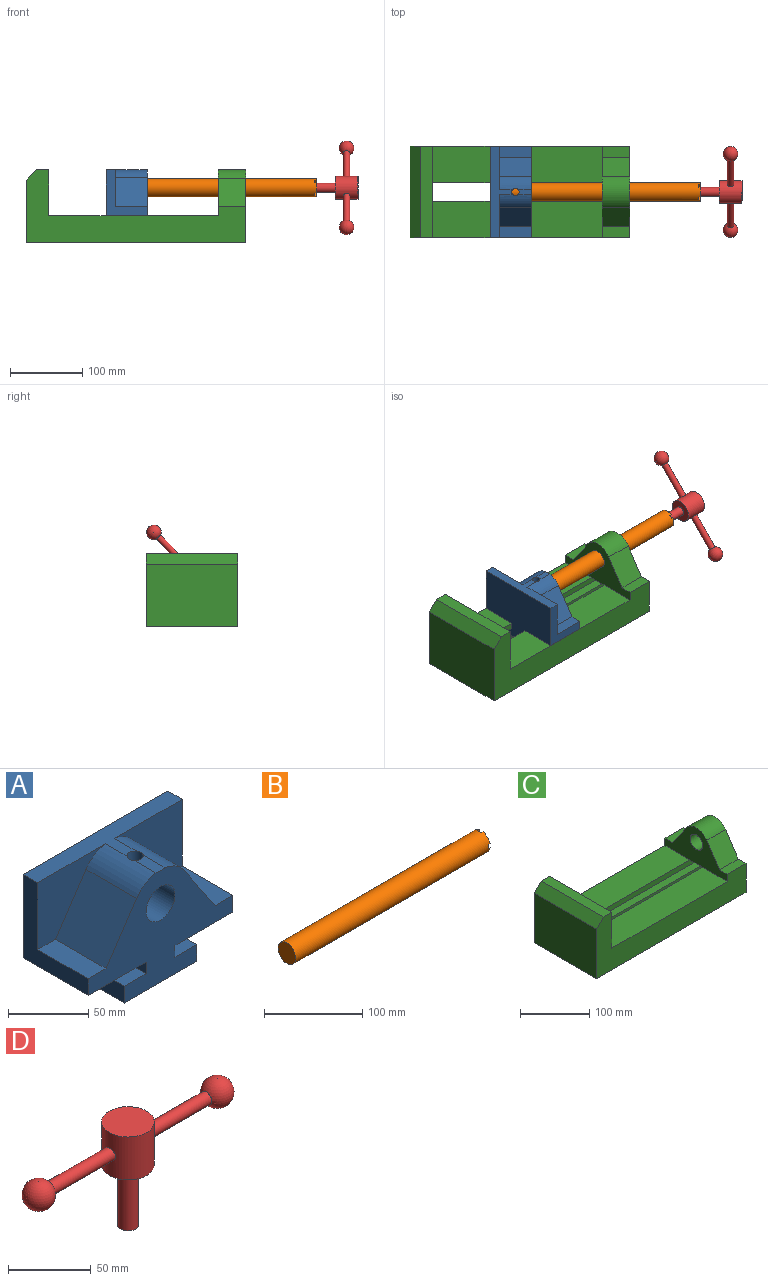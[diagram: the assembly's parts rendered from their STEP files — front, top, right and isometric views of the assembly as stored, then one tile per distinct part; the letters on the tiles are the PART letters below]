
ASSEMBLY  parts=4 mates=3
PART A: 26 faces, bbox 127x57.2x85.1 mm
  f0: plane 127x31.76mm, normal (0,0,1), area 1753.7mm2, adj f2,f3,f14,f15,f18,f20,f22,f25
  f1: plane 19.06x7.94mm, normal (0,0,1), area 140.8mm2, adj f13,f15,f20,f25
  f2: plane 63.5x57.15mm, normal (-1,0,0), area 1371mm2, adj f0,f4,f13,f14,f21,f22
  f3: plane 63.5x57.15mm, normal (1,0,0), area 1371mm2, adj f0,f12,f13,f14,f17,f18
  f4: plane 57.15x50.8mm, normal (0,0,-1), area 2903.2mm2, adj f2,f5,f13,f14
  f5: plane 57.15x8.89mm, normal (-1,0,0), area 508.1mm2, adj f4,f6,f13,f14
  f6: plane 57.15x19.05mm, normal (0,0,1), area 1088.7mm2, adj f5,f7,f13,f14
  f7: plane 57.15x12.7mm, normal (-1,0,0), area 725.8mm2, adj f6,f8,f13,f14
  f8: plane 63.5x57.15mm, normal (0,0,-1), area 3629mm2, adj f7,f9,f13,f14
  f9: plane 57.15x12.7mm, normal (1,0,0), area 725.8mm2, adj f8,f10,f13,f14
  f10: plane 57.15x19.05mm, normal (0,0,1), area 1088.7mm2, adj f9,f11,f13,f14
  f11: plane 57.15x8.89mm, normal (1,0,0), area 508.1mm2, adj f10,f12,f13,f14
  f12: plane 57.15x50.8mm, normal (0,0,-1), area 2903.2mm2, adj f3,f11,f13,f14
  f13: plane 127x85.09mm, normal (0,-1,0), area 5219.4mm2, adj f1,f2,f3,f4,f5,f6,f7,f8
  f14: plane 127x85.09mm, normal (0,1,0), area 9096.8mm2, adj f0,f2,f3,f4,f5,f6,f7,f8
  f15: cylinder r=25.4mm len=44.45mm, axis (0,-1,0), area 923.6mm2, adj f0,f1,f13,f16,f18,f25
  f16: plane 44.45x39.87mm, normal (0.83,0,0.56), area 2135mm2, adj f13,f15,f17,f18
  f17: plane 44.45x15.63mm, normal (0,0,1), area 694.9mm2, adj f3,f13,f16,f18
  f18: plane 59.53x50.8mm, normal (0,-1,0), area 1685.3mm2, adj f0,f3,f15,f16,f17
  f19: plane 44.45x39.87mm, normal (-0.83,0,0.56), area 2135mm2, adj f13,f20,f21,f22
  f20: cylinder r=25.4mm len=44.45mm, axis (0,-1,0), area 923.6mm2, adj f0,f1,f13,f19,f22,f25
  f21: plane 44.45x15.63mm, normal (0,0,1), area 694.9mm2, adj f2,f13,f19,f22
  f22: plane 59.53x50.8mm, normal (0,-1,0), area 1685.3mm2, adj f0,f2,f19,f20,f21
  f23: cylinder r=12.7mm len=44.45mm, axis (0,-1,0), area 3464.1mm2, adj f13,f24,f25
  f24: plane 25.4x25.4mm, normal (0,-1,0), area 506.7mm2, adj f23
  f25: cylinder r=5.08mm len=13.45mm, axis (0,0,1), area 410.4mm2, adj f0,f1,f15,f20,f23
PART B: 20 faces, bbox 279.4x25.4x25.4 mm
  f0: plane 9.9x9.9mm, normal (1,0,0), area 62.3mm2, adj f3,f6,f12,f17
  f1: plane 9.9x9.9mm, normal (1,0,0), area 62.3mm2, adj f3,f6,f14,f18
  f2: plane 9.9x9.9mm, normal (1,0,0), area 62.3mm2, adj f3,f6,f8,f11
  f3: cylinder r=12.7mm len=279.4mm, axis (-1,0,0), area 22243.2mm2, adj f0,f1,f2,f4,f5,f8,f9,f10
  f4: plane 9.9x9.9mm, normal (1,0,0), area 62.3mm2, adj f3,f6,f9,f15
  f5: plane 25.4x25.4mm, normal (-1,0,0), area 506.7mm2, adj f3
  f6: cylinder r=6.35mm len=19.05mm, axis (1,0,0), area 707mm2, adj f0,f1,f2,f4,f7,f8,f9,f10
  f7: plane 12.7x12.7mm, normal (1,0,0), area 126.7mm2, adj f6
  f8: plane 6.62x2.54mm, normal (0,-1,0), area 16.8mm2, adj f2,f3,f6,f10
  f9: plane 6.62x2.54mm, normal (0,1,0), area 16.8mm2, adj f3,f4,f6,f10
  f10: plane 6.88x5.08mm, normal (1,0,0), area 32.7mm2, adj f3,f6,f8,f9
  f11: plane 6.62x2.54mm, normal (0,0,1), area 16.8mm2, adj f2,f3,f6,f13
  f12: plane 6.62x2.54mm, normal (0,0,-1), area 16.8mm2, adj f0,f3,f6,f13
  f13: plane 6.88x5.08mm, normal (1,0,0), area 32.7mm2, adj f3,f6,f11,f12
  f14: plane 6.62x2.54mm, normal (0,0,-1), area 16.8mm2, adj f1,f3,f6,f16
  f15: plane 6.62x2.54mm, normal (0,0,1), area 16.8mm2, adj f3,f4,f6,f16
  f16: plane 6.88x5.08mm, normal (1,0,0), area 32.7mm2, adj f3,f6,f14,f15
  f17: plane 6.62x2.54mm, normal (0,-1,0), area 16.8mm2, adj f0,f3,f6,f19
  f18: plane 6.62x2.54mm, normal (0,1,0), area 16.8mm2, adj f1,f3,f6,f19
  f19: plane 6.88x5.08mm, normal (1,0,0), area 32.7mm2, adj f3,f6,f17,f18
PART C: 28 faces, bbox 304.8x127x101.6 mm
  f0: plane 127x101.6mm, normal (1,0,0), area 7544.1mm2, adj f4,f8,f9,f11,f12,f13,f14,f15
  f1: plane 234.95x50.8mm, normal (0,0,1), area 11935.5mm2, adj f2,f6,f9,f19
  f2: plane 127x63.5mm, normal (-1,0,0), area 4157.1mm2, adj f1,f5,f8,f9,f11,f12,f13,f14
  f3: plane 127x87.31mm, normal (-1,0,0), area 11088.7mm2, adj f4,f8,f9,f10
  f4: plane 304.8x127mm, normal (0,0,-1), area 31774.1mm2, adj f0,f3,f6,f8,f9,f15,f24
  f5: plane 234.95x50.8mm, normal (0,0,1), area 11935.5mm2, adj f2,f6,f8,f20
  f6: plane 127x101.6mm, normal (1,0,0), area 9516.1mm2, adj f1,f4,f5,f7,f8,f9,f15,f16
  f7: plane 127x17.46mm, normal (0,0,1), area 2217.7mm2, adj f6,f8,f9,f10
  f8: plane 304.8x101.6mm, normal (0,-1,0), area 14010.8mm2, adj f0,f2,f3,f4,f5,f6,f7,f10
  f9: plane 304.8x101.6mm, normal (0,1,0), area 14010.8mm2, adj f0,f1,f2,f3,f4,f6,f7,f10
  f10: plane 127x14.29mm, normal (-0.71,0,0.71), area 2566.1mm2, adj f3,f7,f8,f9
  f11: plane 38.1x15.88mm, normal (0,0,1), area 604.8mm2, adj f0,f2,f8,f12
  f12: plane 39.31x38.1mm, normal (0,-0.84,0.55), area 1790.2mm2, adj f0,f2,f11,f13
  f13: cylinder r=25.4mm len=42.88mm, axis (1,0,0), area 1945.5mm2, adj f0,f2,f12,f25
  f14: plane 38.1x25.4mm, normal (0,0,-1), area 967.7mm2, adj f0,f2,f19,f20
  f15: plane 273.05x16.51mm, normal (0,-1,0), area 4508.1mm2, adj f0,f4,f6,f16
  f16: plane 273.05x19.05mm, normal (0,0,1), area 5201.6mm2, adj f0,f6,f15,f17
  f17: plane 273.05x12.7mm, normal (0,-1,0), area 3467.7mm2, adj f0,f6,f16,f18
  f18: plane 273.05x19.05mm, normal (0,0,-1), area 5201.6mm2, adj f0,f6,f17,f19
  f19: plane 273.05x8.89mm, normal (0,-1,0), area 2427.4mm2, adj f0,f1,f6,f14,f18
  f20: plane 273.05x8.89mm, normal (0,1,0), area 2427.4mm2, adj f0,f5,f6,f14,f21
  f21: plane 273.05x19.05mm, normal (0,0,-1), area 5201.6mm2, adj f0,f6,f20,f22
  f22: plane 273.05x12.7mm, normal (0,1,0), area 3467.7mm2, adj f0,f6,f21,f23
  f23: plane 273.05x19.05mm, normal (0,0,1), area 5201.6mm2, adj f0,f6,f22,f24
  f24: plane 273.05x16.51mm, normal (0,1,0), area 4508.1mm2, adj f0,f4,f6,f23
  f25: plane 38.71x38.1mm, normal (0,0.82,0.57), area 1790.2mm2, adj f0,f2,f13,f26
  f26: plane 38.1x15.88mm, normal (0,0,1), area 604.8mm2, adj f0,f2,f9,f25
  f27: cylinder r=12.7mm len=38.1mm, axis (1,0,0), area 3040.2mm2, adj f0,f2
PART D: 9 faces, bbox 172.7x31.8x76.2 mm
  f0: cylinder r=4.45mm len=51.82mm, axis (-1,0,0), area 1438.5mm2, adj f2,f8
  f1: cylinder r=4.45mm len=51.82mm, axis (-1,0,0), area 1438.5mm2, adj f2,f7
  f2: cylinder r=15.88mm len=31.75mm, axis (0,0,-1), area 3041.4mm2, adj f0,f1,f5,f6
  f3: cylinder r=6.35mm len=44.45mm, axis (0,0,-1), area 1773.5mm2, adj f4,f6
  f4: plane 12.7x12.7mm, normal (0,0,-1), area 126.7mm2, adj f3
  f5: plane 31.75x31.75mm, normal (0,0,1), area 791.7mm2, adj f2
  f6: plane 31.75x31.75mm, normal (0,0,-1), area 665.1mm2, adj f2,f3
  f7: sphere r=10.16mm, area 1231.8mm2, adj f1
  f8: sphere r=10.16mm, area 1231.8mm2, adj f0
PLACE A rot(axis=(0,0,1),90deg) t=(-153.28,-94.41,-31.14)mm
PLACE B rot(axis=(1,0,0),46deg) t=(-140.58,-62.66,28.87)mm
PLACE C t=(-264.58,0.84,-47.65)mm fixed
PLACE D rot(axis=(-0.35,0.87,-0.35),98.1deg) t=(119.77,-62.66,28.87)mm
MATE revolute B.f3 <-> A.f15  axis (-1,0,0) through (-140.58,-62.66,28.87)mm
MATE fastened B.f3 <-> D.f2  axis (1,0,0) through (119.77,-62.66,28.87)mm
MATE slider C.f6 <-> A.f14  axis (1,0,0) through (-232.83,-126.16,-9.55)mm
